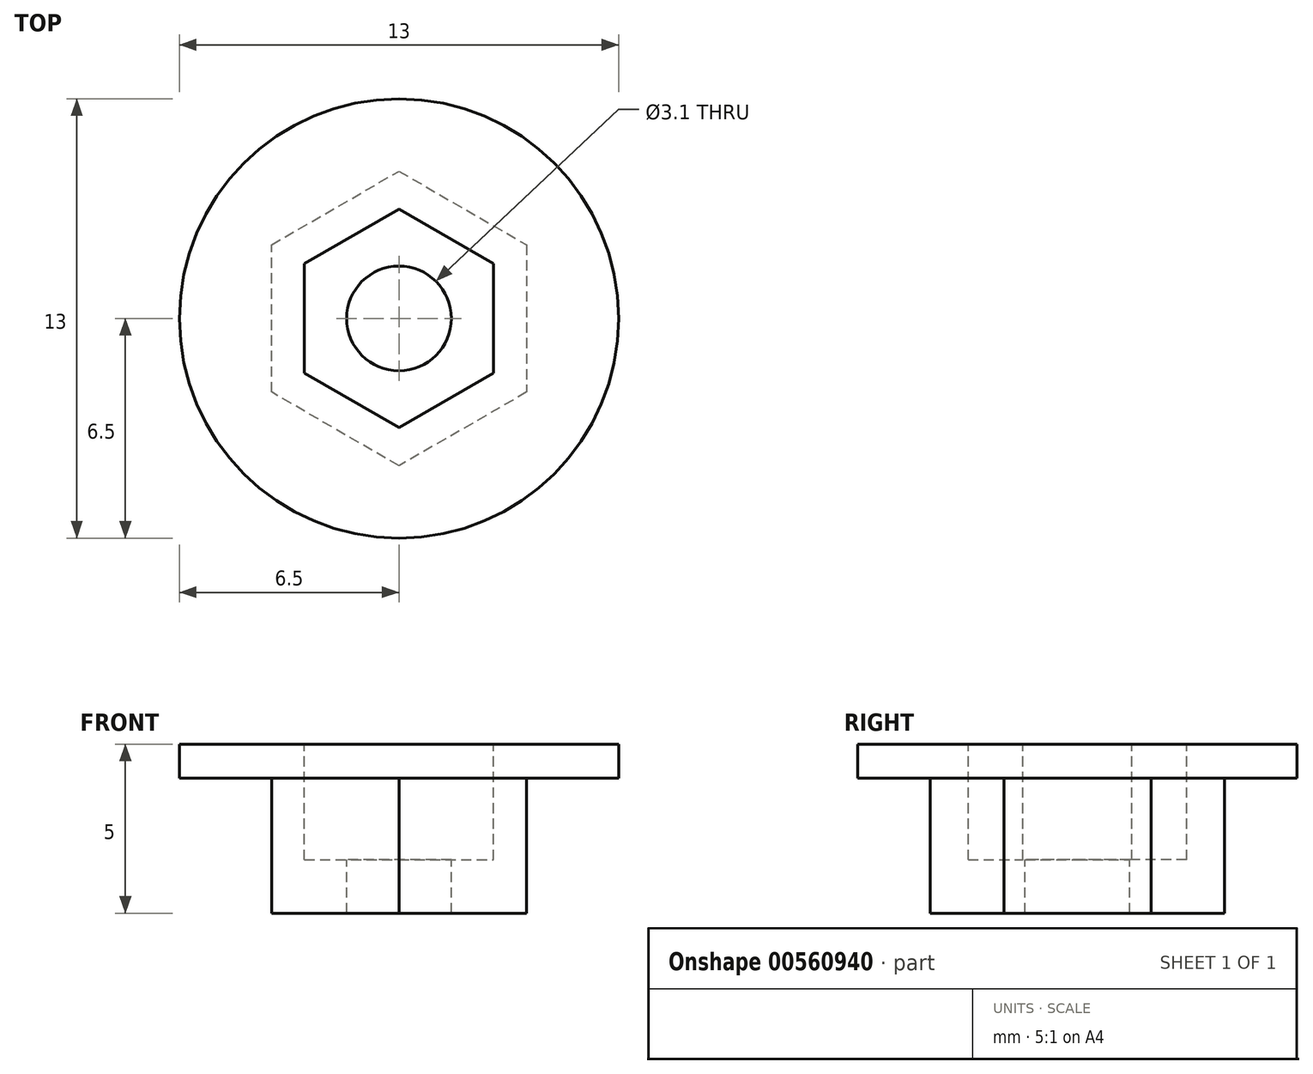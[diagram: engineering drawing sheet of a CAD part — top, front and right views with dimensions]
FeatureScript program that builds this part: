
annotation { "Feature Type Name" : "Feature", "Feature Type Description" : "" }
export const myFeature = defineFeature(function(context is Context, id is Id, definition is map)
    precondition{}
    {
        {
            var Q0;
            Q0=qCreatedBy(makeId("Top.planeOp"),FACE);
            var sketch = newSketch(context, id + "F0", { "sketchPlane" : qUnion([Q0])});
            skCircle(sketch, "E0.cCircle", {"center": v(0, 0) * mm, "radius": 3.78 * mm, "construction": true});
            skLineSegment(sketch, "E0.0", {"start": v(3.78, 2.18) * mm, "end": v(3.78, -2.18) * mm});
            skLineSegment(sketch, "E0.1", {"start": v(3.78, -2.18) * mm, "end": v(0, -4.36) * mm});
            skLineSegment(sketch, "E0.2", {"start": v(0, -4.36) * mm, "end": v(-3.77, -2.18) * mm});
            skLineSegment(sketch, "E0.3", {"start": v(-3.77, -2.18) * mm, "end": v(-3.78, 2.18) * mm});
            skLineSegment(sketch, "E0.4", {"start": v(-3.78, 2.18) * mm, "end": v(0, 4.36) * mm});
            skLineSegment(sketch, "E0.5", {"start": v(0, 4.36) * mm, "end": v(3.78, 2.18) * mm});
            skPoint(sketch, "E0.0.midPoint", {"position": v(3.78, 0) * mm});
            skSolve(sketch);
        }
        {
            var Q0;
            Q0 = qSketchRegion(id + "F0", true);
            extrude(context, id + "F1", {"entities" : qUnion([Q0]), "depth" : 4 * mm, "offsetDistance" : 25 * mm});
        }
        {
            var Q0;
            Q0=makeQuery(id+"F1.opExtrude","CAP_FACE",FACE,{"disambiguationData":[OSD([sQuery(id+"F0.wireOp",EDGE,"E0.0"),sQuery(id+"F0.wireOp",EDGE,"E0.1"),sQuery(id+"F0.wireOp",EDGE,"E0.2"),sQuery(id+"F0.wireOp",EDGE,"E0.3"),sQuery(id+"F0.wireOp",EDGE,"E0.4"),sQuery(id+"F0.wireOp",EDGE,"E0.5")])],"isStart":false});
            var sketch = newSketch(context, id + "F2", { "sketchPlane" : qUnion([Q0])});
            skCircle(sketch, "E1.cCircle", {"center": v(0, 0) * mm, "radius": 2.8 * mm, "construction": true});
            skPoint(sketch, "E1.cCircle.perimeterSnap0", {"position": v(3.78, 0) * mm});
            skLineSegment(sketch, "E1.0", {"start": v(2.8, 1.62) * mm, "end": v(2.8, -1.62) * mm});
            skLineSegment(sketch, "E1.1", {"start": v(2.8, -1.62) * mm, "end": v(0, -3.23) * mm});
            skLineSegment(sketch, "E1.2", {"start": v(0, -3.23) * mm, "end": v(-2.8, -1.62) * mm});
            skLineSegment(sketch, "E1.3", {"start": v(-2.8, -1.62) * mm, "end": v(-2.8, 1.62) * mm});
            skLineSegment(sketch, "E1.4", {"start": v(-2.8, 1.62) * mm, "end": v(0, 3.23) * mm});
            skLineSegment(sketch, "E1.5", {"start": v(0, 3.23) * mm, "end": v(2.8, 1.62) * mm});
            skPoint(sketch, "E1.0.midPoint", {"position": v(2.8, 0) * mm});
            skPoint(sketch, "E1.0.midPoint.positionSnap0", {"position": v(3.78, 0) * mm});
            skSolve(sketch);
        }
        {
            var Q0;
            Q0 = qSketchRegion(id + "F2", true);
            extrude(context, id + "F3", {"entities" : qUnion([Q0]), "operationType" : NewBodyOperationType.REMOVE, "oppositeDirection" : true, "depth" : 2.42 * mm, "offsetDistance" : 25 * mm});
        }
        {
            var Q0;
            Q0=makeQuery(id+"F3.boolean.opBoolean","COPY",FACE,{"derivedFrom":makeQuery(id+"F3.opExtrude","CAP_FACE",FACE,{"disambiguationData":[OSD([sQuery(id+"F2.wireOp",EDGE,"E1.0"),sQuery(id+"F2.wireOp",EDGE,"E1.1"),sQuery(id+"F2.wireOp",EDGE,"E1.2"),sQuery(id+"F2.wireOp",EDGE,"E1.3"),sQuery(id+"F2.wireOp",EDGE,"E1.4"),sQuery(id+"F2.wireOp",EDGE,"E1.5")])],"isStart":false})});
            var sketch = newSketch(context, id + "F4", { "sketchPlane" : qUnion([Q0])});
            skCircle(sketch, "E2", {"center": v(0, 0) * mm, "radius": 1.55 * mm});
            skSolve(sketch);
        }
        {
            var Q0;
            Q0 = qSketchRegion(id + "F4", true);
            extrude(context, id + "F5", {"entities" : qUnion([Q0]), "operationType" : NewBodyOperationType.REMOVE, "oppositeDirection" : true, "depth" : 25 * mm, "offsetDistance" : 25 * mm});
        }
        {
            var Q0;
            Q0=makeQuery(id+"F1.opExtrude","CAP_FACE",FACE,{"disambiguationData":[OSD([sQuery(id+"F0.wireOp",EDGE,"E0.0"),sQuery(id+"F0.wireOp",EDGE,"E0.1"),sQuery(id+"F0.wireOp",EDGE,"E0.2"),sQuery(id+"F0.wireOp",EDGE,"E0.3"),sQuery(id+"F0.wireOp",EDGE,"E0.4"),sQuery(id+"F0.wireOp",EDGE,"E0.5")])],"isStart":false});
            var sketch = newSketch(context, id + "F6", { "sketchPlane" : qUnion([Q0])});
            skCircle(sketch, "E3", {"center": v(0, 0) * mm, "radius": 6.5 * mm});
            skSolve(sketch);
        }
        {
            var Q0;
            Q0 = qSketchRegion(id + "F6", true);
            extrude(context, id + "F7", {"entities" : qUnion([Q0]), "operationType" : NewBodyOperationType.ADD, "depth" : 1 * mm, "offsetDistance" : 25 * mm});
        }
        {
            var Q0;
            Q0=makeQuery(id+"F7.opExtrude","CAP_FACE",FACE,{"disambiguationData":[OSD([sQuery(id+"F6.wireOp",EDGE,"E3")])],"isStart":false});
            var sketch = newSketch(context, id + "F8", { "sketchPlane" : qUnion([Q0])});
            skCircle(sketch, "E4.cCircle", {"center": v(0, 0) * mm, "radius": 2.8 * mm, "construction": true});
            skLineSegment(sketch, "E4.0", {"start": v(2.8, 1.62) * mm, "end": v(2.8, -1.62) * mm});
            skLineSegment(sketch, "E4.1", {"start": v(2.8, -1.62) * mm, "end": v(0, -3.23) * mm});
            skLineSegment(sketch, "E4.2", {"start": v(0, -3.23) * mm, "end": v(-2.8, -1.62) * mm});
            skLineSegment(sketch, "E4.3", {"start": v(-2.8, -1.62) * mm, "end": v(-2.8, 1.62) * mm});
            skLineSegment(sketch, "E4.4", {"start": v(-2.8, 1.62) * mm, "end": v(0, 3.23) * mm});
            skLineSegment(sketch, "E4.5", {"start": v(0, 3.23) * mm, "end": v(2.8, 1.62) * mm});
            skPoint(sketch, "E4.0.midPoint", {"position": v(2.8, 0) * mm});
            skSolve(sketch);
        }
        {
            var Q0;
            Q0 = qSketchRegion(id + "F8", true);
            extrude(context, id + "F9", {"entities" : qUnion([Q0]), "operationType" : NewBodyOperationType.REMOVE, "oppositeDirection" : true, "depth" : 1.8 * mm, "offsetDistance" : 25 * mm});
        }
    });
